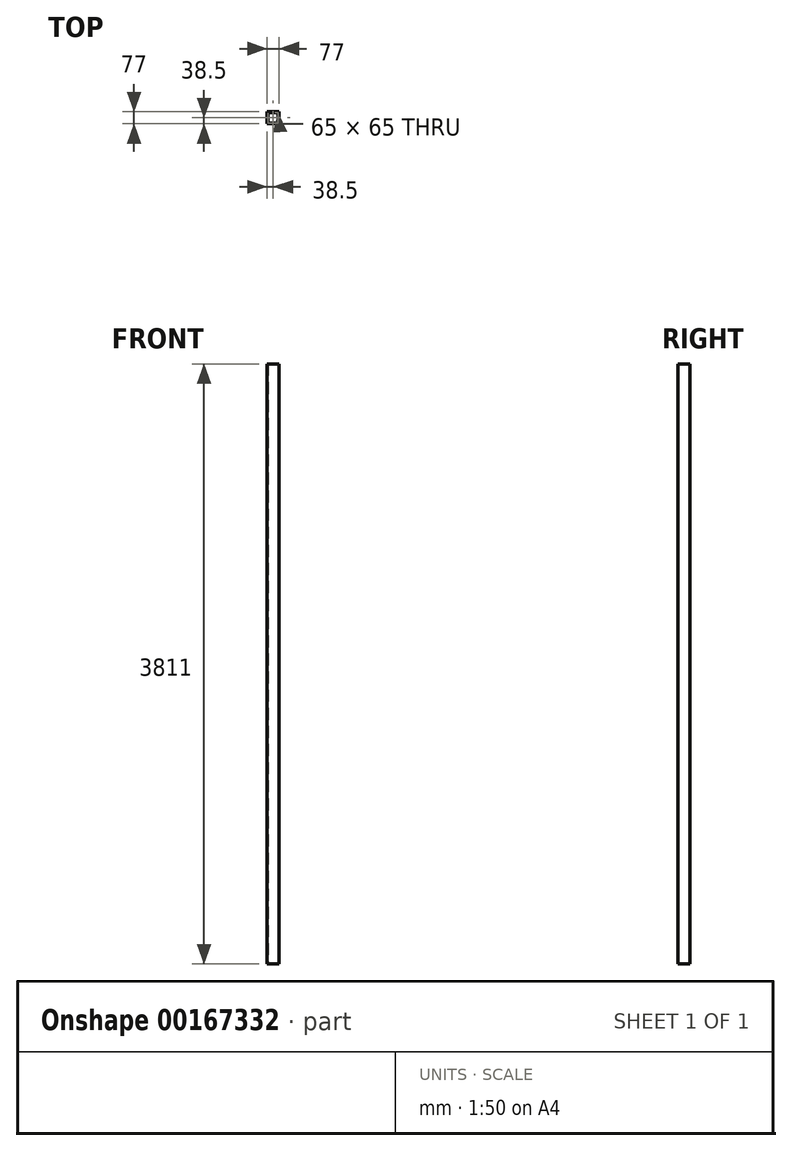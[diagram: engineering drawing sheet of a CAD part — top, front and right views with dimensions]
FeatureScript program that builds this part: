
annotation { "Feature Type Name" : "Feature", "Feature Type Description" : "" }
export const myFeature = defineFeature(function(context is Context, id is Id, definition is map)
    precondition{}
    {
        {
            var Q0;
            Q0=qCreatedBy(makeId("Top.planeOp"),FACE);
            var sketch = newSketch(context, id + "F0", { "sketchPlane" : qUnion([Q0])});
            skLineSegment(sketch, "E0.bottom", {"start": v(0, 0) * mm, "end": v(77, 0) * mm});
            skLineSegment(sketch, "E0.top", {"start": v(0, 77) * mm, "end": v(77, 77) * mm});
            skLineSegment(sketch, "E0.left", {"start": v(0, 0) * mm, "end": v(0, 77) * mm});
            skLineSegment(sketch, "E0.right", {"start": v(77, 0) * mm, "end": v(77, 77) * mm});
            skLineSegment(sketch, "E1.0", {"start": v(6, 6) * mm, "end": v(6, 71) * mm});
            skLineSegment(sketch, "E1.1", {"start": v(6, 6) * mm, "end": v(71, 6) * mm});
            skLineSegment(sketch, "E1.2", {"start": v(71, 6) * mm, "end": v(71, 71) * mm});
            skLineSegment(sketch, "E1.3", {"start": v(6, 71) * mm, "end": v(71, 71) * mm});
            skSolve(sketch);
        }
        {
            var Q0;
            Q0=makeQuery(id+"F0.imprint","IMPRINT",FACE,{"disambiguationData":[TD([[makeQuery(id+"F0.imprint","IMPRINT",EDGE,{"derivedFrom":sQuery(id+"F0.wireOp",EDGE,"E0.bottom")}),1.0]])]});
            extrude(context, id + "F1", {"entities" : qUnion([Q0]), "depth" : 3811 * mm});
        }
    });
